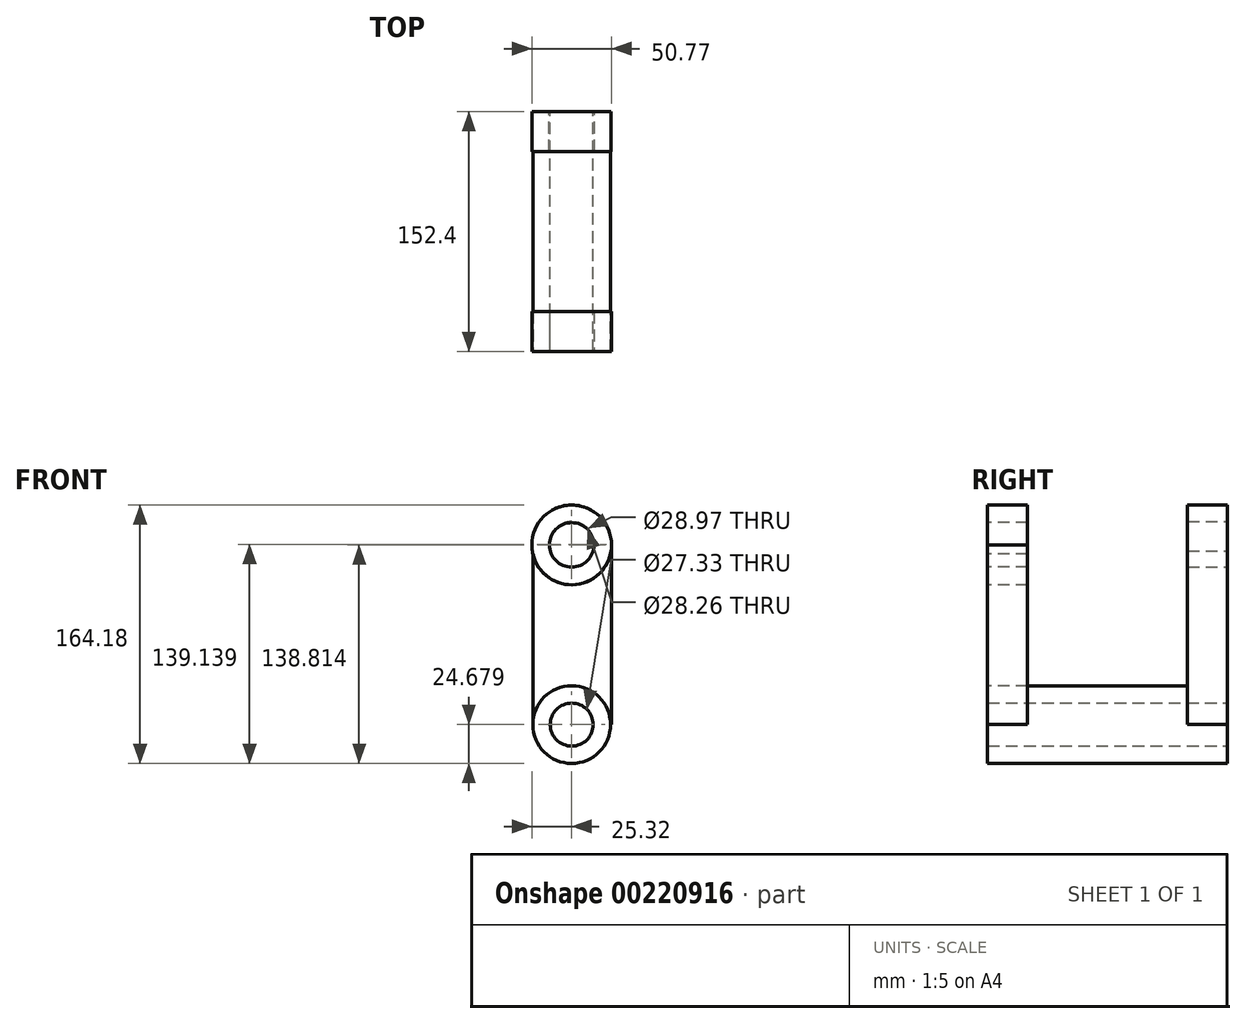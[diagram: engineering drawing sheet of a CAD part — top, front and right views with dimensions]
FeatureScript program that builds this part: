
annotation { "Feature Type Name" : "Feature", "Feature Type Description" : "" }
export const myFeature = defineFeature(function(context is Context, id is Id, definition is map)
    precondition{}
    {
        {
            var Q0;
            Q0=qCreatedBy(makeId("Front.planeOp"),FACE);
            var sketch = newSketch(context, id + "F0", { "sketchPlane" : qUnion([Q0])});
            skCircle(sketch, "E0", {"center": v(0, -61.7) * mm, "radius": 24.68 * mm});
            skCircle(sketch, "E1", {"center": v(0, -61.7) * mm, "radius": 13.67 * mm});
            skLineSegment(sketch, "E2.bottom", {"start": v(24.68, -61.7) * mm, "end": v(25.04, -61.7) * mm});
            skLineSegment(sketch, "E2.left", {"start": v(-24.68, -61.7) * mm, "end": v(-24.68, 52.76) * mm});
            skLineSegment(sketch, "E2.right", {"start": v(25.04, -61.7) * mm, "end": v(25.04, 52.76) * mm});
            skCircle(sketch, "E3", {"center": v(0, 52.76) * mm, "radius": 25.04 * mm});
            skCircle(sketch, "E4", {"center": v(0, 52.76) * mm, "radius": 14.49 * mm});
            skSolve(sketch);
        }
        {
            var Q0;
            Q0=makeQuery(id+"F0.imprint","IMPRINT",FACE,{"disambiguationData":[TD([[makeQuery(id+"F0.imprint","IMPRINT",EDGE,{"derivedFrom":sQuery(id+"F0.wireOp",EDGE,"E4")}),-1.0]])]});
            extrude(context, id + "F1", {"entities" : qUnion([Q0]), "depth" : 25.4 * mm});
        }
        {
            var Q0;
            {var subQ6=sQuery(id+"F0.wireOp",EDGE,"E2.bottom");Q0=makeQuery(id+"F0.imprint","IMPRINT",FACE,{"disambiguationData":[TD([[makeQuery(id+"F0.imprint","IMPRINT",EDGE,{"derivedFrom":subQ6}),1.0]])]});}
            extrude(context, id + "F2", {"entities" : qUnion([Q0]), "operationType" : NewBodyOperationType.ADD, "depth" : 25.4 * mm});
        }
        {
            var Q0;
            Q0=makeQuery(id+"F0.imprint","IMPRINT",FACE,{"disambiguationData":[TD([[makeQuery(id+"F0.imprint","IMPRINT",EDGE,{"derivedFrom":sQuery(id+"F0.wireOp",EDGE,"E1")}),-1.0]])]});
            extrude(context, id + "F3", {"entities" : qUnion([Q0]), "operationType" : NewBodyOperationType.ADD, "depth" : 152.4 * mm});
        }
        {
            var Q0;
            Q0=makeQuery(id+"F3.opExtrude","CAP_FACE",FACE,{"disambiguationData":[OSD([sQuery(id+"F0.wireOp",EDGE,"E0"),sQuery(id+"F0.wireOp",EDGE,"E1")])],"isStart":false});
            var sketch = newSketch(context, id + "F4", { "sketchPlane" : qUnion([Q0])});
            skCircle(sketch, "E5", {"center": v(0, -61.7) * mm, "radius": 13.48 * mm});
            skLineSegment(sketch, "E6.bottom", {"start": v(-24.68, -61.7) * mm, "end": v(-24.36, -61.7) * mm});
            skLineSegment(sketch, "E6.left", {"start": v(-24.68, -61.7) * mm, "end": v(-24.68, 52.43) * mm});
            skLineSegment(sketch, "E6.right", {"start": v(25.45, -61.7) * mm, "end": v(25.45, 52.43) * mm});
            skCircle(sketch, "E7", {"center": v(0, 52.43) * mm, "radius": 14.13 * mm});
            skCircle(sketch, "E8", {"center": v(0, 52.43) * mm, "radius": 25.32 * mm});
            skLineSegment(sketch, "E9.trimOffspring", {"start": v(24.36, -61.7) * mm, "end": v(25.45, -61.7) * mm});
            skLineSegment(sketch, "E10.trimOffspring", {"start": v(25.32, 52.43) * mm, "end": v(25.45, 52.43) * mm});
            skSolve(sketch);
        }
        {
            var Q0;
            {var subQ1=sQuery(id+"F4.wireOp",EDGE,"E6.right");Q0=makeQuery(id+"F4.imprint","IMPRINT",FACE,{"disambiguationData":[TD([[makeQuery(id+"F4.imprint","IMPRINT",EDGE,{"derivedFrom":subQ1}),1.0]])]});}
            extrude(context, id + "F5", {"entities" : qUnion([Q0]), "oppositeDirection" : true, "depth" : 25.4 * mm});
        }
        {
            var Q0;
            Q0=makeQuery(id+"F4.imprint","IMPRINT",FACE,{"disambiguationData":[TD([[makeQuery(id+"F4.imprint","IMPRINT",EDGE,{"derivedFrom":sQuery(id+"F4.wireOp",EDGE,"E7")}),-1.0]])]});
            extrude(context, id + "F6", {"entities" : qUnion([Q0]), "oppositeDirection" : true, "depth" : 25.4 * mm});
        }
    });
